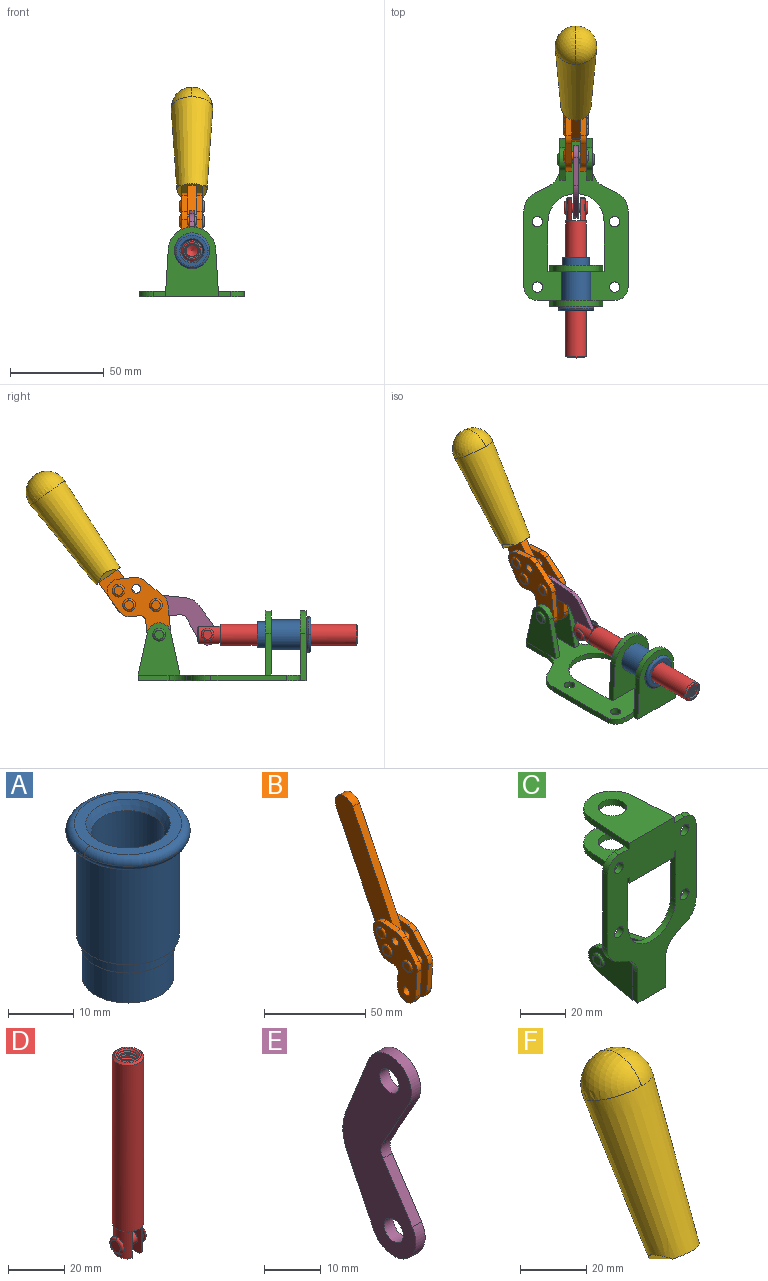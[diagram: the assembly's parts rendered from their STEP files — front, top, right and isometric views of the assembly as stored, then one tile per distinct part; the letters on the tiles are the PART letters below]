
ASSEMBLY  parts=6 mates=6
PART A: 15 faces, bbox 20.6x20.6x28.7 mm
  f0: torus R=8.26mm, axis (0,0,1), area 56.8mm2, adj f1,f10,f12
  f1: torus R=8.26mm, axis (0,0,1), area 56.8mm2, adj f0,f6,f13
  f2: cylinder r=5.59mm len=25.91mm, axis (0,0,1), area 909.6mm2, adj f3,f4
  f3: cone r=6.86mm half-angle=45deg, axis (0,0,-1), area 70.2mm2, adj f2,f14
  f4: cone r=6.47mm half-angle=30deg, axis (0,0,1), area 66.7mm2, adj f2,f13
  f5: cylinder r=7.04mm len=14.07mm, axis (0,0,1), area 252.6mm2, adj f11,f14
  f6: torus R=8.26mm, axis (0,0,1), area 56.8mm2, adj f1,f12,f13
  f7: cylinder r=7.16mm len=14.33mm, axis (0,0,1), area 91.5mm2, adj f9,f11
  f8: cylinder r=7.86mm len=18.42mm, axis (0,0,1), area 909.6mm2, adj f9,f10
  f9: plane 15.72x15.72mm, normal (0,0,-1), area 33mm2, adj f7,f8
  f10: plane 16.51x16.51mm, normal (0,0,-1), area 19.9mm2, adj f0,f8,f12
  f11: plane 14.33x14.33mm, normal (0,0,-1), area 5.7mm2, adj f5,f7
  f12: torus R=8.26mm, axis (0,0,1), area 56.8mm2, adj f0,f6,f10
  f13: plane 16.51x16.51mm, normal (0,0,1), area 82.7mm2, adj f1,f4,f6
  f14: plane 14.07x14.07mm, normal (0,0,-1), area 7.8mm2, adj f3,f5
PART B: 59 faces, bbox 12.9x60.2x99.6 mm
  f0: torus R=2.39mm, axis (-1,0,0), area 14.9mm2, adj f20,f43,f51
  f1: torus R=2.39mm, axis (-1,0,0), area 14.9mm2, adj f19,f42,f51
  f2: torus R=2.39mm, axis (-1,0,0), area 14.9mm2, adj f18,f35,f51
  f3: torus R=2.39mm, axis (-1,0,0), area 14.9mm2, adj f14,f17,f23
  f4: torus R=2.39mm, axis (-1,0,0), area 14.9mm2, adj f13,f16,f23
  f5: torus R=2.39mm, axis (-1,0,0), area 14.9mm2, adj f12,f15,f23
  f6: cylinder r=2.39mm len=4.78mm, axis (1,0,0), area 46.5mm2, adj f48,f50,f51
  f7: cylinder r=2.39mm len=4.78mm, axis (1,0,0), area 46.5mm2, adj f50,f51
  f8: cylinder r=6.35mm len=12.68mm, axis (1,0,0), area 61.8mm2, adj f38,f39,f50,f51
  f9: cylinder r=2.39mm len=4.78mm, axis (-1,0,0), area 70.5mm2, adj f46,f50
  f10: cylinder r=2.39mm len=4.78mm, axis (-1,0,0), area 46.5mm2, adj f23,f45,f46
  f11: cylinder r=2.39mm len=4.78mm, axis (-1,0,0), area 46.5mm2, adj f23,f46
  f12: plane 4.78x4.78mm, normal (1,0,0), area 17.9mm2, adj f5,f15
  f13: plane 4.78x4.78mm, normal (1,0,0), area 17.9mm2, adj f4,f16
  f14: plane 4.78x4.78mm, normal (1,0,0), area 17.9mm2, adj f3,f17
  f15: torus R=2.39mm, axis (-1,0,0), area 14.9mm2, adj f5,f12,f23
  f16: torus R=2.39mm, axis (-1,0,0), area 14.9mm2, adj f4,f13,f23
  f17: torus R=2.39mm, axis (-1,0,0), area 14.9mm2, adj f3,f14,f23
  f18: plane 4.78x4.78mm, normal (-1,0,0), area 17.9mm2, adj f2,f35
  f19: plane 4.78x4.78mm, normal (-1,0,0), area 17.9mm2, adj f1,f42
  f20: plane 4.78x4.78mm, normal (-1,0,0), area 17.9mm2, adj f0,f43
  f21: plane 2.26x0.2mm, normal (1,0,0), area 0.2mm2, adj f31,f44
  f22: plane 2.26x0.2mm, normal (-1,0,0), area 0.2mm2, adj f41,f44
  f23: plane 39.37x30.77mm, normal (1,0,0), area 565.5mm2, adj f3,f4,f5,f10,f11,f15,f16,f17
  f24: cylinder r=6.1mm len=4.15mm, axis (-1,0,0), area 14.7mm2, adj f23,f25,f32,f46
  f25: plane 10.25x9.01mm, normal (0,-0.75,0.66), area 42.3mm2, adj f23,f24,f26,f46
  f26: cylinder r=6.35mm len=4.64mm, axis (-1,0,0), area 15.6mm2, adj f23,f25,f27,f46
  f27: plane 15.84x3.1mm, normal (0,-1,-0.07), area 49.2mm2, adj f23,f26,f28,f46
  f28: cylinder r=6.35mm len=12.68mm, axis (-1,0,0), area 61.8mm2, adj f23,f27,f29,f46
  f29: plane 8.11x3.1mm, normal (0,1,0.07), area 25.2mm2, adj f23,f28,f30,f46
  f30: cylinder r=3.05mm len=3.25mm, axis (-1,0,0), area 14.8mm2, adj f23,f29,f31,f46
  f31: plane 5.99x3.1mm, normal (0,0.07,-1), area 18.6mm2, adj f21,f23,f30,f44,f46
  f32: plane 9.5x3.1mm, normal (0,-0.07,1), area 29.5mm2, adj f23,f24,f33,f46,f47
  f33: cylinder r=6.1mm len=8.63mm, axis (-1,0,0), area 39.1mm2, adj f23,f32,f34,f47
  f34: plane 8.65x3.96mm, normal (0,0.91,-0.42), area 29.5mm2, adj f23,f33,f44,f47
  f35: torus R=2.39mm, axis (-1,0,0), area 14.9mm2, adj f2,f18,f51
  f36: plane 10.25x9.01mm, normal (0,-0.75,0.66), area 42.3mm2, adj f37,f49,f50,f51
  f37: cylinder r=6.35mm len=4.64mm, axis (1,0,0), area 15.6mm2, adj f36,f38,f50,f51
  f38: plane 15.84x3.1mm, normal (0,-1,-0.07), area 49.2mm2, adj f8,f37,f50,f51
  f39: plane 8.11x3.1mm, normal (0,1,0.07), area 25.2mm2, adj f8,f40,f50,f51
  f40: cylinder r=3.05mm len=3.25mm, axis (1,0,0), area 14.8mm2, adj f39,f41,f50,f51
  f41: plane 5.99x3.1mm, normal (0,0.07,-1), area 18.6mm2, adj f22,f40,f44,f50,f51
  f42: torus R=2.39mm, axis (-1,0,0), area 14.9mm2, adj f1,f19,f51
  f43: torus R=2.39mm, axis (-1,0,0), area 14.9mm2, adj f0,f20,f51
  f44: cylinder r=6.35mm len=12.12mm, axis (-1,0,0), area 128.9mm2, adj f21,f22,f23,f31,f34,f41,f46,f47
  f45: plane 2.65x1.35mm, normal (1,0,0), area 1mm2, adj f10,f55
  f46: plane 39.08x20.42mm, normal (-1,0,0), area 412.5mm2, adj f9,f10,f11,f24,f25,f26,f27,f28
  f47: plane 77.62x39.82mm, normal (1,0,0), area 850mm2, adj f32,f33,f34,f44,f53,f54,f55
  f48: plane 2.65x1.35mm, normal (-1,0,0), area 1mm2, adj f6,f55
  f49: cylinder r=6.1mm len=4.15mm, axis (1,0,0), area 14.7mm2, adj f36,f50,f51,f56
  f50: plane 39.08x20.42mm, normal (1,0,0), area 412.5mm2, adj f6,f7,f8,f9,f36,f37,f38,f39
  f51: plane 39.37x30.77mm, normal (-1,0,0), area 565.5mm2, adj f0,f1,f2,f6,f7,f8,f35,f36
  f52: plane 8.65x3.96mm, normal (0,0.91,-0.42), area 29.5mm2, adj f44,f51,f57,f58
  f53: plane 68.49x33.4mm, normal (0,0.9,-0.44), area 358.1mm2, adj f44,f47,f54,f58
  f54: cylinder r=6.35mm len=12.06mm, axis (1,0,0), area 93.7mm2, adj f47,f53,f55,f58
  f55: plane 68.49x33.4mm, normal (0,-0.9,0.44), area 358.1mm2, adj f44,f45,f46,f47,f48,f50,f54,f58
  f56: plane 9.5x3.1mm, normal (0,-0.07,1), area 29.5mm2, adj f49,f50,f51,f57,f58
  f57: cylinder r=6.1mm len=8.63mm, axis (1,0,0), area 39.1mm2, adj f51,f52,f56,f58
  f58: plane 77.62x39.82mm, normal (-1,0,0), area 850mm2, adj f44,f52,f53,f54,f55,f56,f57
PART C: 55 faces, bbox 55.7x37.4x89.8 mm
  f0: torus R=2.41mm, axis (-1,0,0), area 15mm2, adj f11,f15,f25
  f1: torus R=2.41mm, axis (-1,0,0), area 15mm2, adj f10,f12,f22
  f2: cylinder r=2.78mm len=5.56mm, axis (0,-1,0), area 54.2mm2, adj f30,f54
  f3: cylinder r=14.99mm len=29.97mm, axis (0,-1,0), area 145.9mm2, adj f30,f49,f53,f54
  f4: cylinder r=2.78mm len=5.56mm, axis (0,-1,0), area 54.2mm2, adj f30,f54
  f5: cylinder r=2.78mm len=5.56mm, axis (0,-1,0), area 54.2mm2, adj f30,f54
  f6: cylinder r=2.78mm len=5.56mm, axis (0,-1,0), area 54.2mm2, adj f30,f54
  f7: cylinder r=6.35mm len=12.7mm, axis (0,0,1), area 123.6mm2, adj f27,f51
  f8: cylinder r=6.35mm len=12.7mm, axis (0,0,-1), area 124.7mm2, adj f21,f35
  f9: cylinder r=2.41mm len=11.18mm, axis (-1,0,0), area 169.4mm2, adj f16,f19
  f10: plane 4.83x4.83mm, normal (1,0,0), area 18.3mm2, adj f1,f12
  f11: plane 4.83x4.83mm, normal (-1,0,0), area 18.3mm2, adj f0,f15
  f12: torus R=2.41mm, axis (-1,0,0), area 15mm2, adj f1,f10,f22
  f13: cylinder r=6.35mm len=12.41mm, axis (1,0,0), area 53.4mm2, adj f18,f19,f22,f23
  f14: cylinder r=6.35mm len=12.41mm, axis (-1,0,0), area 53.4mm2, adj f16,f17,f24,f25
  f15: torus R=2.41mm, axis (-1,0,0), area 15mm2, adj f0,f11,f25
  f16: plane 27.86x22.35mm, normal (1,0,0), area 425.4mm2, adj f9,f14,f17,f24,f30
  f17: plane 22.86x4.97mm, normal (0,0.21,0.98), area 72.5mm2, adj f14,f16,f25,f30
  f18: plane 22.86x4.97mm, normal (0,0.21,0.98), area 72.5mm2, adj f13,f19,f22,f30
  f19: plane 27.86x22.35mm, normal (-1,0,0), area 425.4mm2, adj f9,f13,f18,f23,f30
  f20: cylinder r=12.7mm len=25.35mm, axis (0,0,-1), area 119.8mm2, adj f21,f34,f35,f36
  f21: plane 34.21x28.07mm, normal (0,0,-1), area 702.4mm2, adj f8,f20,f30,f34,f36
  f22: plane 27.96x22.45mm, normal (1,0,0), area 407.2mm2, adj f1,f12,f13,f18,f23,f30,f42,f43
  f23: plane 22.86x4.97mm, normal (0,0.21,-0.98), area 72.5mm2, adj f13,f19,f22,f44
  f24: plane 22.86x4.97mm, normal (0,0.21,-0.98), area 72.5mm2, adj f14,f16,f25,f44
  f25: plane 27.86x22.35mm, normal (-1,0,0), area 407.1mm2, adj f0,f14,f15,f17,f24,f30,f45,f46
  f26: plane 3.1x0.95mm, normal (0,0,-1), area 2.7mm2, adj f30,f49,f50,f54
  f27: plane 34.21x28.07mm, normal (0,0,1), area 702.4mm2, adj f7,f28,f30,f50,f52
  f28: cylinder r=12.7mm len=25.35mm, axis (0,0,1), area 118.8mm2, adj f27,f50,f51,f52
  f29: plane 3.1x0.95mm, normal (0,0,-1), area 2.7mm2, adj f30,f52,f53,f54
  f30: plane 86.54x55.63mm, normal (0,1,0), area 2362.9mm2, adj f2,f3,f4,f5,f6,f16,f17,f18
  f31: plane 40.56x3.1mm, normal (-1,0,0), area 125.7mm2, adj f30,f32,f48,f54
  f32: cylinder r=7.11mm len=7.11mm, axis (0,-1,0), area 34.6mm2, adj f30,f31,f33,f54
  f33: plane 6.67x3.1mm, normal (0,0,1), area 20.4mm2, adj f30,f32,f34,f54
  f34: plane 25.39x3.13mm, normal (-1,0.06,0), area 79.5mm2, adj f20,f21,f33,f35,f54
  f35: plane 37.31x28.45mm, normal (0,0,1), area 789.9mm2, adj f8,f20,f34,f36,f54
  f36: plane 25.39x3.13mm, normal (1,0.06,0), area 79.5mm2, adj f20,f21,f35,f37,f54
  f37: plane 6.67x3.1mm, normal (0,0,1), area 20.4mm2, adj f30,f36,f38,f54
  f38: cylinder r=7.11mm len=7.11mm, axis (0,-1,0), area 34.6mm2, adj f30,f37,f39,f54
  f39: plane 40.56x3.1mm, normal (1,0,0), area 125.7mm2, adj f30,f38,f40,f54
  f40: cylinder r=11.18mm len=10.16mm, axis (0,-1,0), area 39.5mm2, adj f30,f39,f41,f54
  f41: plane 6.09x3.1mm, normal (0.42,0,-0.91), area 20.8mm2, adj f30,f40,f42,f54
  f42: cylinder r=11.18mm len=9.41mm, axis (0,-1,0), area 37.2mm2, adj f22,f30,f41,f43,f54
  f43: plane 16.5x3.1mm, normal (1,0,0), area 51.1mm2, adj f22,f42,f44,f54
  f44: plane 17.37x3.1mm, normal (0,0,-1), area 53.8mm2, adj f23,f24,f30,f43,f45,f54
  f45: plane 16.5x3.1mm, normal (-1,0,0), area 51.1mm2, adj f25,f44,f46,f54
  f46: cylinder r=11.18mm len=9.41mm, axis (0,-1,0), area 37.2mm2, adj f25,f30,f45,f47,f54
  f47: plane 6.09x3.1mm, normal (-0.42,0,-0.91), area 20.8mm2, adj f30,f46,f48,f54
  f48: cylinder r=11.18mm len=10.16mm, axis (0,-1,0), area 39.5mm2, adj f30,f31,f47,f54
  f49: plane 26.54x3.1mm, normal (-1,0,0), area 82.3mm2, adj f3,f26,f30,f54
  f50: plane 25.39x3.1mm, normal (1,0.06,0), area 78.8mm2, adj f26,f27,f28,f51,f54
  f51: plane 37.31x28.45mm, normal (0,0,-1), area 789.9mm2, adj f7,f28,f50,f52,f54
  f52: plane 25.39x3.1mm, normal (-1,0.06,0), area 78.8mm2, adj f27,f28,f29,f51,f54
  f53: plane 26.54x3.1mm, normal (1,0,0), area 82.3mm2, adj f3,f29,f30,f54
  f54: plane 89.66x55.63mm, normal (0,-1,0), area 2678.5mm2, adj f2,f3,f4,f5,f6,f26,f29,f31
PART D: 48 faces, bbox 12.6x11.1x86.1 mm
  f0: torus R=2.41mm, axis (-1,0,0), area 15mm2, adj f30,f32,f34
  f1: torus R=2.41mm, axis (-1,0,0), area 15mm2, adj f29,f31,f33
  f2: cylinder r=5.54mm len=72.39mm, axis (0,0,1), area 2518.5mm2, adj f3,f4,f42,f43
  f3: cone r=5.54mm half-angle=45deg, axis (0,0,1), area 7.6mm2, adj f2,f5,f41
  f4: cone r=5.54mm half-angle=45deg, axis (0,0,-1), area 34.9mm2, adj f2,f39
  f5: cylinder r=5.08mm len=11.48mm, axis (0,0,1), area 108.3mm2, adj f3,f7,f8,f41
  f6: cylinder r=2.41mm len=4.83mm, axis (-1,0,0), area 71.2mm2, adj f40,f41
  f7: cylinder r=2.41mm len=4.83mm, axis (-1,0,0), area 7.6mm2, adj f5,f34
  f8: cone r=5.08mm half-angle=45deg, axis (0,0,1), area 10.6mm2, adj f5,f37,f41
  f9: cone r=3.98mm half-angle=45deg, axis (0,0,1), area 17.6mm2, adj f27,f39,f45,f46,f47
  f10: cylinder r=2.41mm len=4.83mm, axis (-1,0,0), area 7.6mm2, adj f33,f38
  f11: cylinder r=3.2mm len=6.4mm, axis (0,0,1), area 78.4mm2, adj f12,f28,f44,f45,f47
  f12: cylinder r=3.2mm len=6.4mm, axis (0,0,1), area 10.5mm2, adj f11,f13,f45,f47
  f13: cylinder r=3.2mm len=6.4mm, axis (0,0,1), area 10.5mm2, adj f12,f14,f45,f47
  f14: cylinder r=3.2mm len=6.4mm, axis (0,0,1), area 10.5mm2, adj f13,f15,f45,f47
  f15: cylinder r=3.2mm len=6.4mm, axis (0,0,1), area 10.5mm2, adj f14,f16,f45,f47
  f16: cylinder r=3.2mm len=6.4mm, axis (0,0,1), area 10.5mm2, adj f15,f17,f45,f47
  f17: cylinder r=3.2mm len=6.4mm, axis (0,0,1), area 10.5mm2, adj f16,f18,f45,f47
  f18: cylinder r=3.2mm len=6.4mm, axis (0,0,1), area 10.5mm2, adj f17,f19,f45,f47
  f19: cylinder r=3.2mm len=6.4mm, axis (0,0,1), area 10.5mm2, adj f18,f20,f45,f47
  f20: cylinder r=3.2mm len=6.4mm, axis (0,0,1), area 10.5mm2, adj f19,f21,f45,f47
  f21: cylinder r=3.2mm len=6.4mm, axis (0,0,1), area 10.5mm2, adj f20,f22,f45,f47
  f22: cylinder r=3.2mm len=6.4mm, axis (0,0,1), area 10.5mm2, adj f21,f23,f45,f47
  f23: cylinder r=3.2mm len=6.4mm, axis (0,0,1), area 10.5mm2, adj f22,f24,f45,f47
  f24: cylinder r=3.2mm len=6.4mm, axis (0,0,1), area 10.5mm2, adj f23,f25,f45,f47
  f25: cylinder r=3.2mm len=6.4mm, axis (0,0,1), area 10.5mm2, adj f24,f26,f45,f47
  f26: cylinder r=3.2mm len=6.4mm, axis (0,0,1), area 10.5mm2, adj f25,f27,f45,f47
  f27: cylinder r=3.2mm len=6.4mm, axis (0,0,1), area 7.4mm2, adj f9,f26,f45,f47
  f28: cone r=3.2mm half-angle=60deg, axis (0,0,1), area 37.2mm2, adj f11
  f29: plane 4.83x4.83mm, normal (-1,0,0), area 18.3mm2, adj f1,f31
  f30: plane 4.83x4.83mm, normal (1,0,0), area 18.3mm2, adj f0,f32
  f31: torus R=2.41mm, axis (-1,0,0), area 15mm2, adj f1,f29,f33
  f32: torus R=2.41mm, axis (-1,0,0), area 15mm2, adj f0,f30,f34
  f33: plane 6.83x6.83mm, normal (1,0,0), area 18.3mm2, adj f1,f10,f31
  f34: plane 6.83x6.83mm, normal (-1,0,0), area 18.3mm2, adj f0,f7,f32
  f35: cone r=5.08mm half-angle=45deg, axis (0,0,1), area 10.6mm2, adj f36,f38,f40
  f36: plane 7.25x1.97mm, normal (0,0,-1), area 10mm2, adj f35,f40
  f37: plane 7.25x1.97mm, normal (0,0,-1), area 10mm2, adj f8,f41
  f38: cylinder r=5.08mm len=11.48mm, axis (0,0,1), area 108.3mm2, adj f10,f35,f40,f42
  f39: plane 9.55x9.55mm, normal (0,0,1), area 22mm2, adj f4,f9
  f40: plane 12.76x10.09mm, normal (1,0,0), area 95.7mm2, adj f6,f35,f36,f38,f42,f43
  f41: plane 12.76x10.09mm, normal (-1,0,0), area 95.7mm2, adj f3,f5,f6,f8,f37,f43
  f42: cone r=5.54mm half-angle=45deg, axis (0,0,1), area 7.6mm2, adj f2,f38,f40
  f43: plane 11.07x4.7mm, normal (0,0,-1), area 50.4mm2, adj f2,f40,f41
  f44: plane 0.89x0.62mm, normal (-1,0,0), area 0.3mm2, adj f11,f45,f46,f47
  f45: bspline ~24.8x7.63mm, area 266.6mm2, adj f9,f11,f12,f13,f14,f15,f16,f17
  f46: bspline ~24.87x7.63mm, area 73.6mm2, adj f9,f44,f45,f47
  f47: bspline ~24.98x7.63mm, area 272.5mm2, adj f9,f11,f12,f13,f14,f15,f16,f17
PART E: 12 faces, bbox 2.3x18.2x42.8 mm
  f0: cylinder r=2.4mm len=4.8mm, axis (1,0,0), area 34.9mm2, adj f4,f11
  f1: cylinder r=10.41mm len=8.47mm, axis (1,0,0), area 20.2mm2, adj f4,f9,f10,f11
  f2: cylinder r=3.05mm len=3.16mm, axis (1,0,0), area 7.7mm2, adj f4,f6,f7,f11
  f3: cylinder r=2.4mm len=4.8mm, axis (1,0,0), area 34.9mm2, adj f4,f11
  f4: plane 42.81x18.23mm, normal (-1,0,0), area 414.1mm2, adj f0,f1,f2,f3,f5,f6,f7,f8
  f5: cylinder r=5.54mm len=10.67mm, axis (1,0,0), area 41.8mm2, adj f4,f6,f10,f11
  f6: plane 11.66x6.53mm, normal (0,-0.87,-0.49), area 30.9mm2, adj f2,f4,f5,f11
  f7: plane 11.17x7.33mm, normal (0,-0.84,0.55), area 30.9mm2, adj f2,f4,f8,f11
  f8: cylinder r=5.54mm len=10.51mm, axis (1,0,0), area 41.8mm2, adj f4,f7,f9,f11
  f9: plane 13.67x6.67mm, normal (0,0.9,-0.44), area 35.1mm2, adj f1,f4,f8,f11
  f10: plane 14.1x5.7mm, normal (0,0.93,0.37), area 35.1mm2, adj f1,f4,f5,f11
  f11: plane 42.81x18.23mm, normal (1,0,0), area 414.1mm2, adj f0,f1,f2,f3,f5,f6,f7,f8
PART F: 11 faces, bbox 22.3x42.6x64.5 mm
  f0: sphere r=11.13mm, area 411.4mm2, adj f1,f8
  f1: cone r=11.11mm half-angle=3.3deg, axis (0,0.44,0.9), area 3251.8mm2, adj f0,f7,f8,f9,f10
  f2: cylinder r=6.16mm len=11.7mm, axis (1,0,0), area 89.5mm2, adj f3,f4,f5,f6
  f3: plane 60.23x36.75mm, normal (-1,0,0), area 763.6mm2, adj f2,f4,f6,f10
  f4: plane 51.37x25.05mm, normal (0,0.9,-0.44), area 264.2mm2, adj f2,f3,f5,f10
  f5: plane 60.23x36.75mm, normal (1,0,0), area 763.6mm2, adj f2,f4,f6,f10
  f6: plane 51.37x25.05mm, normal (0,-0.9,0.44), area 264.2mm2, adj f2,f3,f5,f10
  f7: plane 9.95x5.95mm, normal (0.71,-0.31,-0.64), area 25.8mm2, adj f1,f10
  f8: sphere r=11.13mm, area 411.4mm2, adj f0,f1
  f9: plane 9.95x5.95mm, normal (-0.71,-0.31,-0.64), area 25.8mm2, adj f1,f10
  f10: plane 14.27x11.38mm, normal (0,-0.44,-0.9), area 106.7mm2, adj f1,f3,f4,f5,f6,f7,f9
PLACE A rot(axis=(1,0,0),90deg) t=(0,9.43,0)mm
PLACE B rot(axis=(-1,0,0),10deg) t=(0,22.86,60.49)mm
PLACE C rot(axis=(1,0,0),90deg) t=(0,9.43,0)mm fixed
PLACE D rot(axis=(1,0,0),90deg) t=(0,31.11,0)mm
PLACE E rot(axis=(1,0,0),121.8deg) t=(0,41.76,11.86)mm
PLACE F rot(axis=(-1,0,0),10deg) t=(-0.04,22.86,60.49)mm
MATE slider D.f2 <-> A.f12  axis (0,-1,0) through (0,-27.67,24.61)mm
MATE fastened F.f2 <-> B.f54  axis (1,0,0) through (-2.35,102.33,102.1)mm
MATE fastened C.f7 <-> A.f2  axis (0,-1,0) through (0,-36.96,24.61)mm
MATE revolute E.f5 <-> D.f6  axis (1,0,0) through (0,15.64,24.61)mm
MATE revolute B.f7 <-> C.f0  axis (1,0,0) through (0,41.52,24.61)mm
MATE revolute E.f3 <-> B.f4  axis (-1,0,0) through (0,43.18,40.4)mm
